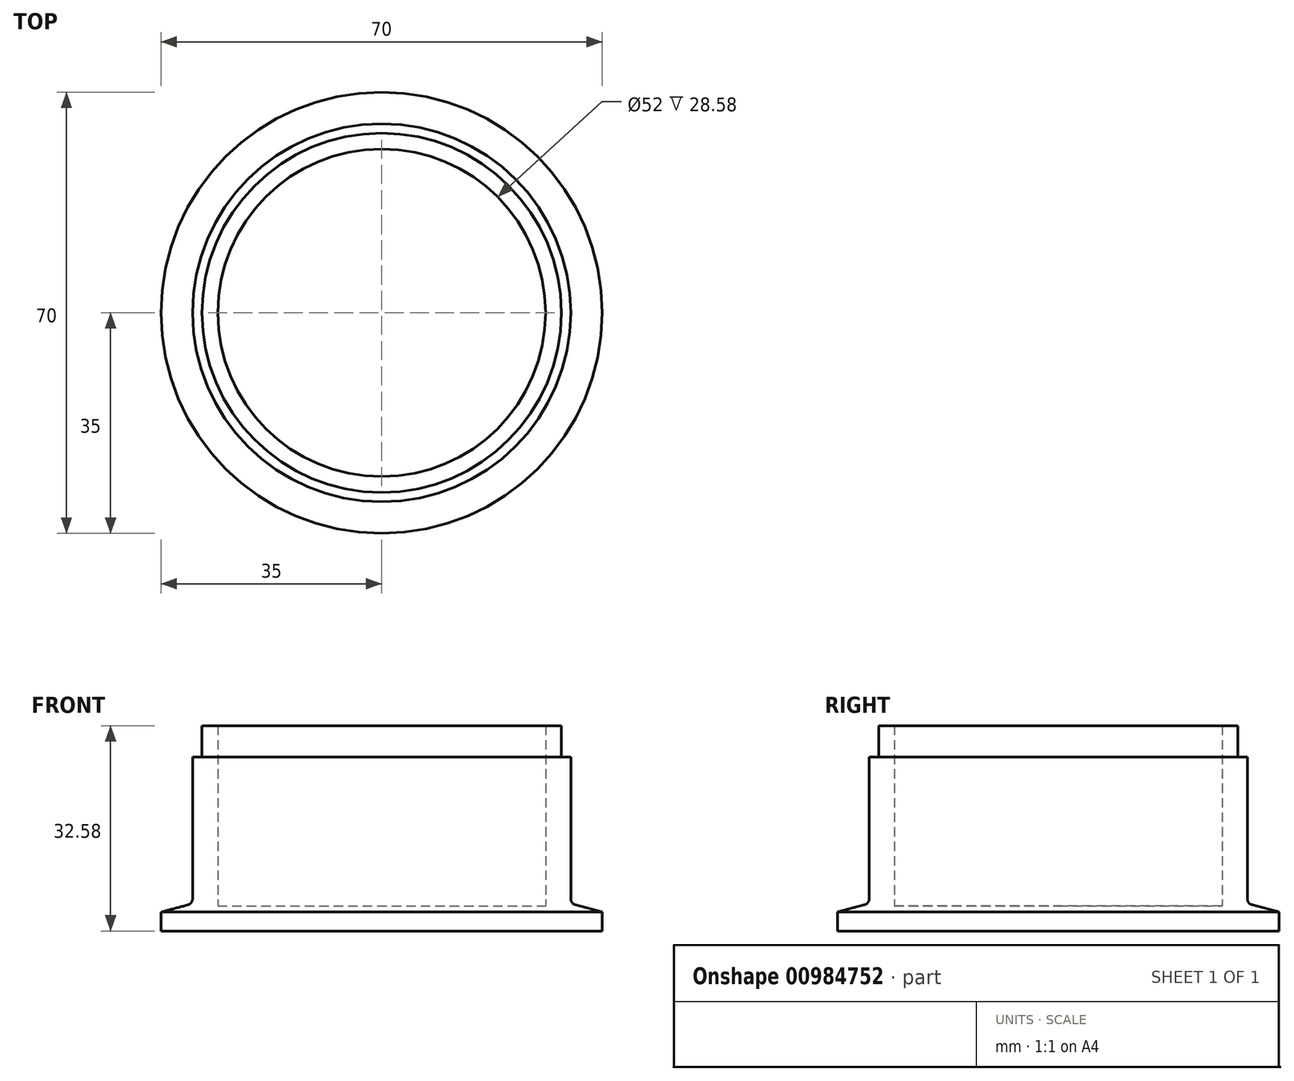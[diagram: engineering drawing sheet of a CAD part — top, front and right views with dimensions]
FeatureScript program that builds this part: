
annotation { "Feature Type Name" : "Feature", "Feature Type Description" : "" }
export const myFeature = defineFeature(function(context is Context, id is Id, definition is map)
    precondition{}
    {
        {
            var Q0;
            Q0=qCreatedBy(makeId("Front.planeOp"),FACE);
            var sketch = newSketch(context, id + "F0", { "sketchPlane" : qUnion([Q0])});
            skLineSegment(sketch, "E0", {"start": v(0, 0) * mm, "end": v(0, 38.36) * mm, "construction": true});
            skLineSegment(sketch, "E1.bottom", {"start": v(0, 0) * mm, "end": v(35, 0) * mm});
            skLineSegment(sketch, "E1.top", {"start": v(26, 32.58) * mm, "end": v(30, 32.58) * mm});
            skLineSegment(sketch, "E1.left", {"start": v(0, 0) * mm, "end": v(0, 32.58) * mm});
            skLineSegment(sketch, "E1.right", {"start": v(30, 4.34) * mm, "end": v(30, 32.58) * mm});
            skLineSegment(sketch, "E2.top", {"start": v(30, 4.34) * mm, "end": v(35, 3) * mm});
            skLineSegment(sketch, "E2.right", {"start": v(35, 0) * mm, "end": v(35, 3) * mm});
            skLineSegment(sketch, "E3", {"start": v(26, 32.58) * mm, "end": v(26, 4) * mm});
            skLineSegment(sketch, "E4", {"start": v(26, 4) * mm, "end": v(0, 4) * mm});
            skSolve(sketch);
        }
        {
            var Q0;
            Q0 = qSketchRegion(id + "F0", true);
            var Q1;
            Q1=sQuery(id+"F0.wireOp",EDGE,"E1.left");
            revolve(context, id + "F1", {"surfaceOperationType" : NewSurfaceOperationType.NEW, "entities" : qUnion([Q0]), "axis" : qUnion([Q1]), "revolveType" : RevolveType.FULL});
        }
        {
            var Q0;
            Q0=makeQuery(id+"F1.opRevolve","SWEPT_FACE",FACE,{"disambiguationData":[OSD([sQuery(id+"F0.wireOp",EDGE,"E1.top")])]});
            var sketch = newSketch(context, id + "F2", { "sketchPlane" : qUnion([Q0])});
            skCircle(sketch, "E5", {"center": v(0, 0) * mm, "radius": 28.5 * mm});
            skCircle(sketch, "E6", {"center": v(0, 0) * mm, "radius": 30 * mm});
            skSolve(sketch);
        }
        {
            var Q0;
            Q0 = qSketchRegion(id + "F2", true);
            extrude(context, id + "F3", {"entities" : qUnion([Q0]), "operationType" : NewBodyOperationType.REMOVE, "oppositeDirection" : true, "depth" : 5 * mm, "offsetDistance" : 25 * mm});
        }
        {
            var Q0;
            Q0=makeQuery(id+"F1.opRevolve","SWEPT_EDGE",EDGE,{"disambiguationData":[OSD([sQuery(id+"F0.wireOp",EDGE,"E1.right"),sQuery(id+"F0.wireOp",EDGE,"E2.top")])]});
            fillet(context, id + "F4", {"entities" : qUnion([Q0]), "radius" : 1 * mm, "tangentPropagation" : true, "allowEdgeOverflow" : false});
        }
    });
